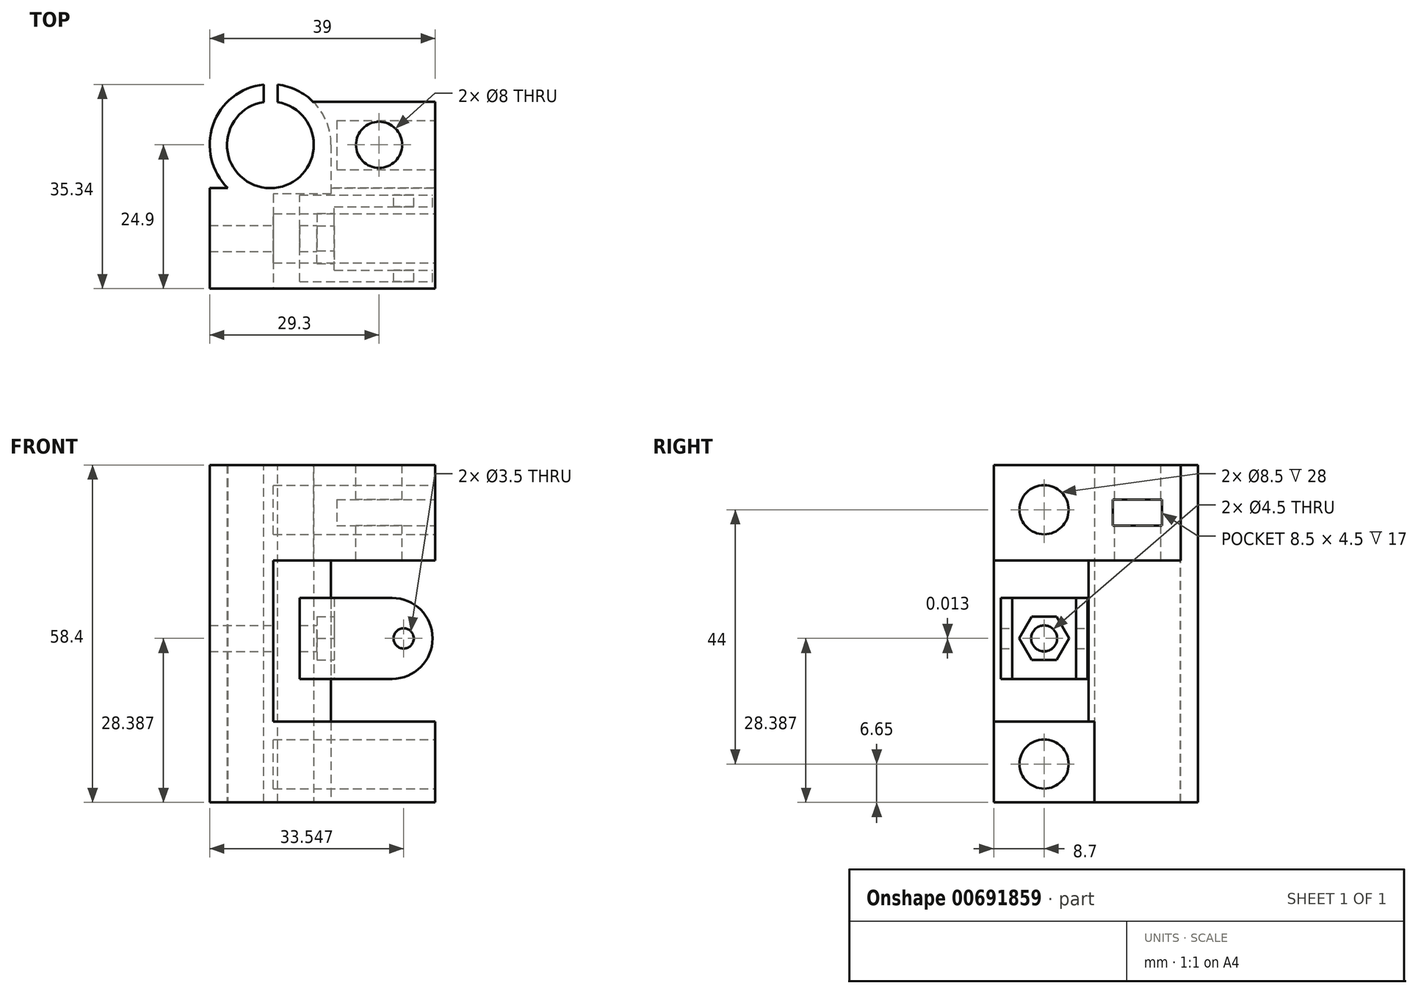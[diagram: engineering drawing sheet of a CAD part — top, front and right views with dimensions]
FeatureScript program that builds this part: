
annotation { "Feature Type Name" : "Feature", "Feature Type Description" : "" }
export const myFeature = defineFeature(function(context is Context, id is Id, definition is map)
    precondition{}
    {
        {
            var Q0;
            Q0=qCreatedBy(makeId("Top.planeOp"),FACE);
            var sketch = newSketch(context, id + "F0", { "sketchPlane" : qUnion([Q0])});
            skLineSegment(sketch, "E0.bottom", {"start": v(19.5, 8.7) * mm, "end": v(-19.5, 8.7) * mm});
            skLineSegment(sketch, "E0.top", {"start": v(19.5, -8.7) * mm, "end": v(-19.5, -8.7) * mm});
            skLineSegment(sketch, "E0.left", {"start": v(19.5, 8.7) * mm, "end": v(19.5, -8.7) * mm});
            skLineSegment(sketch, "E0.right", {"start": v(-19.5, 8.7) * mm, "end": v(-19.5, -8.7) * mm});
            skPoint(sketch, "E0.middle", {"position": v(0, 0) * mm});
            skCircle(sketch, "E1", {"center": v(-9, 16.2) * mm, "radius": 7.5 * mm});
            skLineSegment(sketch, "E2", {"start": v(-19.5, 6.34) * mm, "end": v(-19.5, 42.3) * mm});
            skCircle(sketch, "E3", {"center": v(-9, 16.2) * mm, "radius": 10.5 * mm});
            skLineSegment(sketch, "E4", {"start": v(-19.5, 16.2) * mm, "end": v(-19.5, 8.7) * mm});
            skLineSegment(sketch, "E5", {"start": v(1.5, 16.24) * mm, "end": v(1.5, 8.7) * mm});
            skCircle(sketch, "E6", {"center": v(9, 16.2) * mm, "radius": 3 * mm});
            skSolve(sketch);
        }
        {
            var Q0;
            {var subQ4=sQuery(id+"F0.wireOp",EDGE,"E1");Q0=makeQuery(id+"F0.imprint","IMPRINT",FACE,{"disambiguationData":[TD([[makeQuery(id+"F0.imprint","IMPRINT",EDGE,{"derivedFrom":subQ4}),-1.0]])]});}
            var Q1;
            {var subQ0=sQuery(id+"F0.wireOp",EDGE,"E4");Q1=makeQuery(id+"F0.imprint","IMPRINT",FACE,{"disambiguationData":[TD([[makeQuery(id+"F0.imprint","IMPRINT",EDGE,{"derivedFrom":subQ0}),1.0]])]});}
            var Q2;
            {var subQ0=sQuery(id+"F0.wireOp",EDGE,"E5");Q2=makeQuery(id+"F0.imprint","IMPRINT",FACE,{"disambiguationData":[TD([[makeQuery(id+"F0.imprint","IMPRINT",EDGE,{"derivedFrom":subQ0}),-1.0]])]});}
            var Q3;
            Q3=makeQuery(id+"F0.imprint","IMPRINT",FACE,{"disambiguationData":[TD([[makeQuery(id+"F0.imprint","IMPRINT",EDGE,{"derivedFrom":sQuery(id+"F0.wireOp",EDGE,"E0.top")}),-1.0]])]});
            var Q4;
            {var subQ0=sQuery(id+"F0.wireOp",EDGE,"E0.bottom");var subQ1=makeQuery(id+"F0.imprint","INTERSECT",VERTEX,{"derivedFrom":[subQ0,sQuery(id+"F0.wireOp",EDGE,"E1")]});Q4=makeQuery(id+"F0.imprint","IMPRINT",FACE,{"disambiguationData":[TD([[makeQuery(id+"F0.imprint","IMPRINT",EDGE,{"disambiguationData":[TD([[subQ1,1.0]])],"derivedFrom":subQ0}),1.0]])]});}
            extrude(context, id + "F1", {"entities" : qUnion([Q0, Q1, Q2, Q3, Q4]), "depth" : 58.4 * mm, "offsetDistance" : 25 * mm});
        }
        {
            var Q0;
            Q0=makeQuery(id+"F1.opExtrude","CAP_FACE",FACE,{"disambiguationData":[OSD([sQuery(id+"F0.wireOp",EDGE,"E0.bottom"),sQuery(id+"F0.wireOp",EDGE,"E0.top"),sQuery(id+"F0.wireOp",EDGE,"E0.left"),sQuery(id+"F0.wireOp",EDGE,"E0.right"),sQuery(id+"F0.wireOp",EDGE,"E1"),sQuery(id+"F0.wireOp",EDGE,"E2"),sQuery(id+"F0.wireOp",EDGE,"E3"),sQuery(id+"F0.wireOp",EDGE,"E4"),sQuery(id+"F0.wireOp",EDGE,"E5")])],"isStart":false});
            var sketch = newSketch(context, id + "F2", { "sketchPlane" : qUnion([Q0])});
            skLineSegment(sketch, "E7", {"start": v(-9, 16.2) * mm, "end": v(9, 16.16) * mm, "construction": true});
            skLineSegment(sketch, "E8.bottom", {"start": v(19.5, 8.7) * mm, "end": v(-1.5, 8.7) * mm});
            skLineSegment(sketch, "E8.top", {"start": v(19.5, 23.62) * mm, "end": v(-1.5, 23.62) * mm});
            skLineSegment(sketch, "E8.left", {"start": v(19.5, 8.7) * mm, "end": v(19.5, 23.62) * mm});
            skLineSegment(sketch, "E8.right", {"start": v(-1.5, 8.7) * mm, "end": v(-1.5, 23.62) * mm});
            skPoint(sketch, "E8.middle", {"position": v(9, 16.16) * mm});
            skSolve(sketch);
        }
        {
            var Q0;
            {var subQ1=sQuery(id+"F2.wireOp",EDGE,"E8.top");Q0=makeQuery(id+"F2.imprint","IMPRINT",FACE,{"disambiguationData":[TD([[makeQuery(id+"F2.imprint","IMPRINT",EDGE,{"derivedFrom":subQ1}),1.0]])]});}
            extrude(context, id + "F3", {"entities" : qUnion([Q0]), "oppositeDirection" : true, "depth" : 16.5 * mm, "offsetDistance" : 25 * mm});
        }
        {
            var Q0;
            Q0=makeQuery(id+"F3.opExtrude","SWEPT_FACE",FACE,{"disambiguationData":[OSD([sQuery(id+"F2.wireOp",EDGE,"E8.left")])]});
            var sketch = newSketch(context, id + "F4", { "sketchPlane" : qUnion([Q0])});
            skLineSegment(sketch, "E9.bottom", {"start": v(20.4, 52.4) * mm, "end": v(11.9, 52.4) * mm});
            skLineSegment(sketch, "E9.top", {"start": v(20.4, 47.9) * mm, "end": v(11.9, 47.9) * mm});
            skLineSegment(sketch, "E9.left", {"start": v(20.4, 52.4) * mm, "end": v(20.4, 47.9) * mm});
            skLineSegment(sketch, "E9.right", {"start": v(11.9, 52.4) * mm, "end": v(11.9, 47.9) * mm});
            skPoint(sketch, "E9.middle", {"position": v(16.16, 50.15) * mm});
            skPoint(sketch, "E9.middle.positionSnap0", {"position": v(23.62, 50.15) * mm});
            skPoint(sketch, "E9.middle.positionSnap1", {"position": v(16.16, 58.4) * mm});
            skPoint(sketch, "E9.centerSnap0", {"position": v(23.62, 50.15) * mm});
            skPoint(sketch, "E9.centerSnap1", {"position": v(16.16, 58.4) * mm});
            skSolve(sketch);
        }
        {
            var Q0;
            Q0=makeQuery(id+"F4.imprint","IMPRINT",FACE,{"disambiguationData":[TD([[makeQuery(id+"F4.imprint","IMPRINT",EDGE,{"derivedFrom":sQuery(id+"F4.wireOp",EDGE,"E9.bottom")}),1.0]])]});
            extrude(context, id + "F5", {"entities" : qUnion([Q0]), "operationType" : NewBodyOperationType.REMOVE, "oppositeDirection" : true, "depth" : 17 * mm, "offsetDistance" : 25 * mm});
        }
        {
            var Q0;
            Q0=makeQuery(id+"F3.opExtrude","CAP_FACE",FACE,{"disambiguationData":[OSD([sQuery(id+"F0.wireOp",EDGE,"E3"),sQuery(id+"F0.wireOp",EDGE,"E5"),sQuery(id+"F2.wireOp",EDGE,"E8.bottom"),sQuery(id+"F2.wireOp",EDGE,"E8.top"),sQuery(id+"F2.wireOp",EDGE,"E8.left"),sQuery(id+"F2.wireOp",EDGE,"E8.right")])],"isStart":true});
            var sketch = newSketch(context, id + "F6", { "sketchPlane" : qUnion([Q0])});
            skLineSegment(sketch, "E10", {"start": v(-9, 16.2) * mm, "end": v(9.8, 16.2) * mm, "construction": true});
            skCircle(sketch, "E11", {"center": v(9.8, 16.2) * mm, "radius": 4 * mm});
            skSolve(sketch);
        }
        {
            var Q0;
            Q0=makeQuery(id+"F6.imprint","IMPRINT",FACE,{"disambiguationData":[TD([[makeQuery(id+"F6.imprint","IMPRINT",EDGE,{"derivedFrom":sQuery(id+"F6.wireOp",EDGE,"E11")}),1.0]])]});
            extrude(context, id + "F7", {"entities" : qUnion([Q0]), "operationType" : NewBodyOperationType.REMOVE, "oppositeDirection" : true, "depth" : 25 * mm, "offsetDistance" : 25 * mm});
        }
        {
            var Q0;
            Q0=makeQuery(id+"F1.opExtrude","SWEPT_FACE",FACE,{"disambiguationData":[OSD([sQuery(id+"F0.wireOp",EDGE,"E0.left")])]});
            var sketch = newSketch(context, id + "F8", { "sketchPlane" : qUnion([Q0])});
            skLineSegment(sketch, "E12.bottom", {"start": v(8.7, 41.9) * mm, "end": v(-8.7, 41.9) * mm});
            skLineSegment(sketch, "E12.top", {"start": v(8.7, 14) * mm, "end": v(-8.7, 14) * mm});
            skLineSegment(sketch, "E12.left", {"start": v(8.7, 41.9) * mm, "end": v(8.7, 14) * mm});
            skLineSegment(sketch, "E12.right", {"start": v(-8.7, 41.9) * mm, "end": v(-8.7, 14) * mm});
            skCircle(sketch, "E13", {"center": v(0, 50.65) * mm, "radius": 4.25 * mm});
            skCircle(sketch, "E14", {"center": v(0, 6.65) * mm, "radius": 4.25 * mm});
            skSolve(sketch);
        }
        {
            var Q0;
            Q0=makeQuery(id+"F8.imprint","IMPRINT",FACE,{"disambiguationData":[TD([[makeQuery(id+"F8.imprint","IMPRINT",EDGE,{"derivedFrom":sQuery(id+"F8.wireOp",EDGE,"E12.bottom")}),1.0]])]});
            var Q1;
            Q1=makeQuery(id+"F8.imprint","IMPRINT",FACE,{"disambiguationData":[TD([[makeQuery(id+"F8.imprint","IMPRINT",EDGE,{"derivedFrom":sQuery(id+"F8.wireOp",EDGE,"E14")}),1.0]])]});
            var Q2;
            Q2=makeQuery(id+"F8.imprint","IMPRINT",FACE,{"disambiguationData":[TD([[makeQuery(id+"F8.imprint","IMPRINT",EDGE,{"derivedFrom":sQuery(id+"F8.wireOp",EDGE,"E13")}),1.0]])]});
            extrude(context, id + "F9", {"entities" : qUnion([Q0, Q1, Q2]), "operationType" : NewBodyOperationType.REMOVE, "oppositeDirection" : true, "depth" : 28 * mm, "offsetDistance" : 25 * mm});
        }
        {
            var Q0;
            Q0=makeQuery(id+"F9.boolean.opBoolean","COPY",FACE,{"derivedFrom":makeQuery(id+"F9.opExtrude","CAP_FACE",FACE,{"disambiguationData":[OSD([sQuery(id+"F8.wireOp",EDGE,"E12.bottom"),sQuery(id+"F8.wireOp",EDGE,"E12.top"),sQuery(id+"F8.wireOp",EDGE,"E12.left"),sQuery(id+"F8.wireOp",EDGE,"E12.right")])],"isStart":false})});
            var sketch = newSketch(context, id + "F10", { "sketchPlane" : qUnion([Q0])});
            skCircle(sketch, "E15", {"center": v(0, 28.4) * mm, "radius": 2.25 * mm});
            skSolve(sketch);
        }
        {
            var Q0;
            Q0=makeQuery(id+"F10.imprint","IMPRINT",FACE,{"disambiguationData":[TD([[makeQuery(id+"F10.imprint","IMPRINT",EDGE,{"derivedFrom":sQuery(id+"F10.wireOp",EDGE,"E15")}),1.0]])]});
            extrude(context, id + "F11", {"entities" : qUnion([Q0]), "operationType" : NewBodyOperationType.REMOVE, "oppositeDirection" : true, "depth" : 25 * mm, "offsetDistance" : 25 * mm});
        }
        {
            var Q0;
            Q0=makeQuery(id+"F1.opExtrude","CAP_FACE",FACE,{"disambiguationData":[OSD([sQuery(id+"F0.wireOp",EDGE,"E0.bottom"),sQuery(id+"F0.wireOp",EDGE,"E0.top"),sQuery(id+"F0.wireOp",EDGE,"E0.left"),sQuery(id+"F0.wireOp",EDGE,"E0.right"),sQuery(id+"F0.wireOp",EDGE,"E1"),sQuery(id+"F0.wireOp",EDGE,"E2"),sQuery(id+"F0.wireOp",EDGE,"E3"),sQuery(id+"F0.wireOp",EDGE,"E4"),sQuery(id+"F0.wireOp",EDGE,"E5")])],"isStart":false});
            var sketch = newSketch(context, id + "F12", { "sketchPlane" : qUnion([Q0])});
            skLineSegment(sketch, "E16.bottom", {"start": v(-10.13, 27.77) * mm, "end": v(-7.75, 27.77) * mm});
            skLineSegment(sketch, "E16.top", {"start": v(-10.13, 22.37) * mm, "end": v(-7.75, 22.37) * mm});
            skLineSegment(sketch, "E16.left", {"start": v(-10.13, 27.77) * mm, "end": v(-10.13, 22.37) * mm});
            skLineSegment(sketch, "E16.right", {"start": v(-7.75, 27.77) * mm, "end": v(-7.75, 22.37) * mm});
            skSolve(sketch);
        }
        {
            var Q0;
            {var subQ0=sQuery(id+"F12.wireOp",EDGE,"E16.left");var subQ1=makeQuery(id+"F1.opExtrude","CAP_EDGE",EDGE,{"disambiguationData":[OSD([sQuery(id+"F0.wireOp",EDGE,"E3")])],"isStart":false});var subQ2=makeQuery(id+"F12.imprint","INTERSECT",VERTEX,{"derivedFrom":[subQ1,subQ0]});Q0=makeQuery(id+"F12.imprint","IMPRINT",FACE,{"disambiguationData":[TD([[makeQuery(id+"F12.imprint","IMPRINT",EDGE,{"disambiguationData":[TD([[subQ2,-1.0]])],"derivedFrom":subQ0}),1.0]])]});}
            extrude(context, id + "F13", {"entities" : qUnion([Q0]), "operationType" : NewBodyOperationType.REMOVE, "oppositeDirection" : true, "depth" : 60 * mm, "offsetDistance" : 25 * mm});
        }
        {
            var Q0;
            Q0=qCreatedBy(makeId("Front.planeOp"),FACE);
            var sketch = newSketch(context, id + "F14", { "sketchPlane" : qUnion([Q0])});
            skLineSegment(sketch, "E17.bottom", {"start": v(-46.65, -26.51) * mm, "end": v(-23.65, -26.51) * mm});
            skLineSegment(sketch, "E17.top", {"start": v(-46.65, -40.51) * mm, "end": v(-23.65, -40.51) * mm});
            skLineSegment(sketch, "E17.left", {"start": v(-46.65, -26.51) * mm, "end": v(-46.65, -40.51) * mm});
            skLineSegment(sketch, "E17.right", {"start": v(-23.65, -26.51) * mm, "end": v(-23.65, -40.51) * mm});
            skLineSegment(sketch, "E18", {"start": v(-23.65, -33.51) * mm, "end": v(-28.65, -33.51) * mm, "construction": true});
            skCircle(sketch, "E19", {"center": v(-28.65, -33.51) * mm, "radius": 1.75 * mm});
            skSolve(sketch);
        }
        {
            var Q0;
            Q0=makeQuery(id+"F14.imprint","IMPRINT",FACE,{"disambiguationData":[TD([[makeQuery(id+"F14.imprint","IMPRINT",EDGE,{"derivedFrom":sQuery(id+"F14.wireOp",EDGE,"E17.bottom")}),-1.0]])]});
            extrude(context, id + "F15", {"entities" : qUnion([Q0]), "depth" : 15 * mm, "offsetDistance" : 25 * mm});
        }
        {
            var Q0;
            Q0=makeQuery(id+"F15.opExtrude","SWEPT_FACE",FACE,{"disambiguationData":[OSD([sQuery(id+"F14.wireOp",EDGE,"E17.right")])]});
            var sketch = newSketch(context, id + "F16", { "sketchPlane" : qUnion([Q0])});
            skLineSegment(sketch, "E20.bottom", {"start": v(-13, -26.51) * mm, "end": v(-2, -26.51) * mm});
            skLineSegment(sketch, "E20.top", {"start": v(-13, -40.51) * mm, "end": v(-2, -40.51) * mm});
            skLineSegment(sketch, "E20.left", {"start": v(-13, -26.51) * mm, "end": v(-13, -40.51) * mm});
            skLineSegment(sketch, "E20.right", {"start": v(-2, -26.51) * mm, "end": v(-2, -40.51) * mm});
            skSolve(sketch);
        }
        {
            var Q0;
            Q0=makeQuery(id+"F16.imprint","IMPRINT",FACE,{"disambiguationData":[TD([[makeQuery(id+"F16.imprint","IMPRINT",EDGE,{"derivedFrom":sQuery(id+"F16.wireOp",EDGE,"E20.bottom")}),-1.0]])]});
            extrude(context, id + "F17", {"entities" : qUnion([Q0]), "operationType" : NewBodyOperationType.REMOVE, "oppositeDirection" : true, "depth" : 17 * mm, "offsetDistance" : 25 * mm});
        }
        {
            var Q0;
            {var subQ0=sQuery(id+"F14.wireOp",EDGE,"E17.bottom");var subQ1=sQuery(id+"F14.wireOp",EDGE,"E17.right");Q0=makeQuery(id+"F17.boolean.opBoolean","SPLIT",EDGE,{"disambiguationData":[TD([makeQuery(id+"F17.opExtrude","SWEPT_FACE",FACE,{"disambiguationData":[OSD([sQuery(id+"F16.wireOp",EDGE,"E20.left")])]})])],"derivedFrom":makeQuery(id+"F15.opExtrude","SWEPT_EDGE",EDGE,{"disambiguationData":[OSD([subQ0,subQ1])]})});}
            var Q1;
            {var subQ0=sQuery(id+"F14.wireOp",EDGE,"E17.right");var subQ1=sQuery(id+"F14.wireOp",EDGE,"E17.top");Q1=makeQuery(id+"F17.boolean.opBoolean","SPLIT",EDGE,{"disambiguationData":[TD([makeQuery(id+"F17.opExtrude","SWEPT_FACE",FACE,{"disambiguationData":[OSD([sQuery(id+"F16.wireOp",EDGE,"E20.left")])]})])],"derivedFrom":makeQuery(id+"F15.opExtrude","SWEPT_EDGE",EDGE,{"disambiguationData":[OSD([subQ1,subQ0])]})});}
            var Q2;
            {var subQ0=sQuery(id+"F14.wireOp",EDGE,"E17.bottom");var subQ1=sQuery(id+"F14.wireOp",EDGE,"E17.right");Q2=makeQuery(id+"F17.boolean.opBoolean","SPLIT",EDGE,{"disambiguationData":[TD([makeQuery(id+"F17.opExtrude","SWEPT_FACE",FACE,{"disambiguationData":[OSD([sQuery(id+"F16.wireOp",EDGE,"E20.right")])]})])],"derivedFrom":makeQuery(id+"F15.opExtrude","SWEPT_EDGE",EDGE,{"disambiguationData":[OSD([subQ0,subQ1])]})});}
            var Q3;
            {var subQ0=sQuery(id+"F14.wireOp",EDGE,"E17.right");var subQ1=sQuery(id+"F14.wireOp",EDGE,"E17.top");Q3=makeQuery(id+"F17.boolean.opBoolean","SPLIT",EDGE,{"disambiguationData":[TD([makeQuery(id+"F17.opExtrude","SWEPT_FACE",FACE,{"disambiguationData":[OSD([sQuery(id+"F16.wireOp",EDGE,"E20.right")])]})])],"derivedFrom":makeQuery(id+"F15.opExtrude","SWEPT_EDGE",EDGE,{"disambiguationData":[OSD([subQ1,subQ0])]})});}
            fillet(context, id + "F18", {"entities" : qUnion([Q0, Q1, Q2, Q3]), "radius" : 7 * mm, "tangentPropagation" : true, "allowEdgeOverflow" : false});
        }
        {
            var Q0;
            Q0=makeQuery(id+"F17.boolean.opBoolean","COPY",FACE,{"derivedFrom":makeQuery(id+"F17.opExtrude","CAP_FACE",FACE,{"disambiguationData":[OSD([sQuery(id+"F16.wireOp",EDGE,"E20.bottom"),sQuery(id+"F16.wireOp",EDGE,"E20.top"),sQuery(id+"F16.wireOp",EDGE,"E20.left"),sQuery(id+"F16.wireOp",EDGE,"E20.right")])],"isStart":false})});
            var sketch = newSketch(context, id + "F19", { "sketchPlane" : qUnion([Q0])});
            skLineSegment(sketch, "E21", {"start": v(-7.5, -26.51) * mm, "end": v(-7.5, -40.51) * mm, "construction": true});
            skCircle(sketch, "E22", {"center": v(-7.5, -33.51) * mm, "radius": 2.25 * mm});
            skSolve(sketch);
        }
        {
            var Q0;
            Q0=makeQuery(id+"F19.imprint","IMPRINT",FACE,{"disambiguationData":[TD([[makeQuery(id+"F19.imprint","IMPRINT",EDGE,{"derivedFrom":sQuery(id+"F19.wireOp",EDGE,"E22")}),1.0]])]});
            extrude(context, id + "F20", {"entities" : qUnion([Q0]), "operationType" : NewBodyOperationType.REMOVE, "oppositeDirection" : true, "depth" : 25 * mm, "offsetDistance" : 25 * mm});
        }
        {
            var Q0;
            Q0=makeQuery(id+"F17.boolean.opBoolean","COPY",FACE,{"derivedFrom":makeQuery(id+"F17.opExtrude","CAP_FACE",FACE,{"disambiguationData":[OSD([sQuery(id+"F16.wireOp",EDGE,"E20.bottom"),sQuery(id+"F16.wireOp",EDGE,"E20.top"),sQuery(id+"F16.wireOp",EDGE,"E20.left"),sQuery(id+"F16.wireOp",EDGE,"E20.right")])],"isStart":false})});
            var sketch = newSketch(context, id + "F21", { "sketchPlane" : qUnion([Q0])});
            skCircle(sketch, "E23.cCircle", {"center": v(-7.5, -33.51) * mm, "radius": 4.33 * mm, "construction": true});
            skLineSegment(sketch, "E23.0", {"start": v(-3.17, -33.51) * mm, "end": v(-5.33, -37.26) * mm});
            skLineSegment(sketch, "E23.1", {"start": v(-5.33, -37.26) * mm, "end": v(-9.67, -37.26) * mm});
            skLineSegment(sketch, "E23.2", {"start": v(-9.67, -37.26) * mm, "end": v(-11.83, -33.51) * mm});
            skLineSegment(sketch, "E23.3", {"start": v(-11.83, -33.51) * mm, "end": v(-9.67, -29.76) * mm});
            skLineSegment(sketch, "E23.4", {"start": v(-9.67, -29.76) * mm, "end": v(-5.33, -29.76) * mm});
            skLineSegment(sketch, "E23.5", {"start": v(-5.33, -29.76) * mm, "end": v(-3.17, -33.51) * mm});
            skSolve(sketch);
        }
        {
            var Q0;
            Q0=makeQuery(id+"F21.imprint","IMPRINT",FACE,{"disambiguationData":[TD([[makeQuery(id+"F21.imprint","IMPRINT",EDGE,{"derivedFrom":sQuery(id+"F21.wireOp",EDGE,"E23.0")}),-1.0]])]});
            extrude(context, id + "F22", {"entities" : qUnion([Q0]), "operationType" : NewBodyOperationType.REMOVE, "oppositeDirection" : true, "depth" : 3 * mm, "offsetDistance" : 25 * mm});
        }
        {
            var Q0;
            Q0=makeQuery(id+"F15.opExtrude","SWEPT_BODY",BODY,{"disambiguationData":[OSD([sQuery(id+"F14.wireOp",EDGE,"E17.bottom"),sQuery(id+"F14.wireOp",EDGE,"E17.top"),sQuery(id+"F14.wireOp",EDGE,"E17.left"),sQuery(id+"F14.wireOp",EDGE,"E17.right"),sQuery(id+"F14.wireOp",EDGE,"E19")])]});
            transform(context, id + "F23", {"entities" : qUnion([Q0]), "transformType" : TransformType.TRANSLATION_3D, "dx" : 42.7 * mm, "dy" : 7.5 * mm, "dz" : 61.9 * mm, "makeCopy" : false});
        }
        {
            var Q0;
            Q0=makeQuery(id+"F9.boolean.opBoolean","COPY",FACE,{"derivedFrom":makeQuery(id+"F9.opExtrude","CAP_FACE",FACE,{"disambiguationData":[OSD([sQuery(id+"F8.wireOp",EDGE,"E12.bottom"),sQuery(id+"F8.wireOp",EDGE,"E12.top"),sQuery(id+"F8.wireOp",EDGE,"E12.left"),sQuery(id+"F8.wireOp",EDGE,"E12.right")])],"isStart":false})});
            var sketch = newSketch(context, id + "F24", { "sketchPlane" : qUnion([Q0])});
            skLineSegment(sketch, "E24.bottom", {"start": v(7.7, 41.9) * mm, "end": v(8.7, 41.9) * mm});
            skLineSegment(sketch, "E24.top", {"start": v(7.7, 14) * mm, "end": v(8.7, 14) * mm});
            skLineSegment(sketch, "E24.left", {"start": v(7.7, 41.9) * mm, "end": v(7.7, 14) * mm});
            skLineSegment(sketch, "E24.right", {"start": v(8.7, 41.9) * mm, "end": v(8.7, 14) * mm});
            skSolve(sketch);
        }
        {
            var Q0;
            Q0 = qSketchRegion(id + "F24", true);
            extrude(context, id + "F25", {"entities" : qUnion([Q0]), "operationType" : NewBodyOperationType.ADD, "depth" : 10 * mm, "offsetDistance" : 25 * mm});
        }
    });
